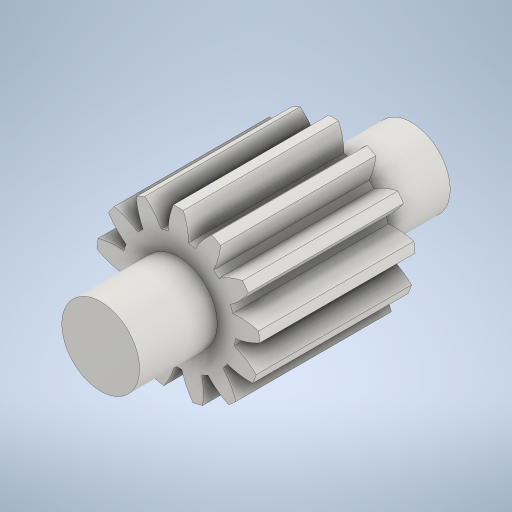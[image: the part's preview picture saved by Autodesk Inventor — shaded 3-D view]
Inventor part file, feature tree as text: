
AUTODESK INVENTOR PART (.ipt)
format: ipt  version: 2023.2 (Build 272271000, 271)  size: 389,632 bytes
history: native  units: mm (DEFAULTED — no unit token found)
features: plane x3, other x3, sketch x3, extrude x2
ambient origin geometry x8: Origin, YZ Plane, XZ Plane, XY Plane, X Axis, Y Axis, Z Axis, Center Point
bodies: Solid1 (feature_tree)
feature tree (11):
  extrude  "Extrusion1"  Depth=10.0mm TaperAngle=0.0deg
  plane  "Work Plane2"
  plane  "Work Plane8"
  plane  "Work Plane9"
  other  "Spur Gear"
  extrude  "Extrusion2"  Depth=10.0mm TaperAngle=0.0deg
  sketch  "Sketch1"  dims[d0=10.503525mm d1=10.0mm d2=0.0mm]
  sketch  "Sketch2"  dims[d3=9.1mm d4=10.0mm d5=0.0mm]
  other  "Srf1"
  sketch  "Sketch3"  dims[d16=12.604893mm d17=0.0mm d34=2.41661mm d39=0.0mm d41=0.0mm d43=12.604893mm d46=12.604893mm d47=0.0mm d48=0.0mm d49=5.0mm d50=5.0mm d51=15.0mm d52=0.0mm d53=0.0mm]
  other  "Pitch Diameter"
